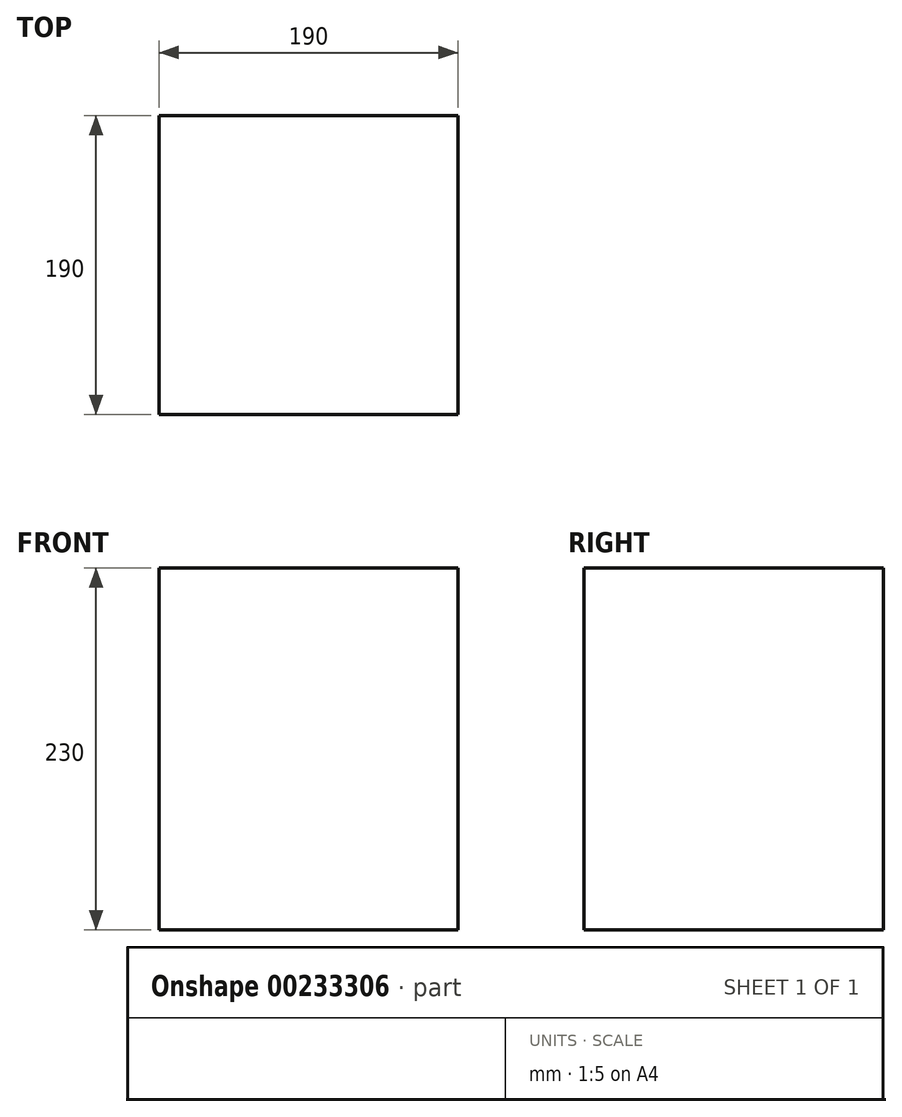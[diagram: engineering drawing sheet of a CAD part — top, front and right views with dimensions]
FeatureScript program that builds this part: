
annotation { "Feature Type Name" : "Feature", "Feature Type Description" : "" }
export const myFeature = defineFeature(function(context is Context, id is Id, definition is map)
    precondition{}
    {
        {
            var Q0;
            Q0=qCreatedBy(makeId("Front.planeOp"),FACE);
            var sketch = newSketch(context, id + "F0", { "sketchPlane" : qUnion([Q0])});
            skLineSegment(sketch, "E0", {"start": v(-128.17, 178.25) * mm, "end": v(61.83, 178.25) * mm});
            skLineSegment(sketch, "E1", {"start": v(61.83, 178.25) * mm, "end": v(61.83, -51.75) * mm});
            skLineSegment(sketch, "E2", {"start": v(61.83, -51.75) * mm, "end": v(-128.17, -51.75) * mm});
            skLineSegment(sketch, "E3", {"start": v(-128.17, -51.75) * mm, "end": v(-128.17, 178.25) * mm});
            skSolve(sketch);
        }
        {
            var Q0;
            Q0=makeQuery(id+"F0.imprint","IMPRINT",FACE,{"disambiguationData":[TD([[makeQuery(id+"F0.imprint","IMPRINT",EDGE,{"derivedFrom":sQuery(id+"F0.wireOp",EDGE,"E0")}),-1.0]])]});
            extrude(context, id + "F1", {"entities" : qUnion([Q0]), "depth" : 190 * mm});
        }
    });
